# Revit family: Dryer_Weight-Rated_Milnor_M115-Gas
name_source: partatom
category: Mechanical Equipment
units: mm (PartAtom-declared; Revit-internal decimal feet)

## family parameters
Always vertical = No
Classification Number = 23.45.70.11.14.17
Cut with Voids When Loaded = No
Maintain Annotation Orientation = No
Part Type = Normal
Room Calculation Point = No
Round Connector Dimension = Use Radius
Shared = No
Work Plane-Based = Yes

## types (9) — shared parameters
Assembly Code = E1010610
Capacity = 115 lbs Dry Weight
Cylinder Depth = 3' - 5 1/4"
Cylinder Diameter = 3' - 6"
Cylinder Volume = 33.1 CF
Default Elevation = 0' - 0"
Description = Milnor Commercial Laundry Dryer - Gas Model M115 as Specified
Door Base from FF = 2' - 3 1/2"
Door Opening = 2' - 7 3/8"
Door Opening Depth = 3' - 1 7/8"
Door Thickness = 0' - 2"
Electrical CL from CL = 0' - 2"
Electrical CL from FF = 6' - 0 1/2"
Electrical CL from Side = 1' - 1 3/4"
Exhaust CL from FF = 1' - 2 9/16"
Exhaust CL from Side = 0' - 8 1/4"
Exhaust Diameter = 1' - 2"
FSS Water Connection CL from FF = 5' - 7 3/8"
FSS Water Connection Diameter = 0' - 0 3/4"
FSS Water Connection from Side = 0' - 2 3/4"
Gas Connection CL from FF = 6' - 0 1/4"
Gas Connection Diameter = 0' - 1"
Gas Connection from Side = 2' - 9 1/4"
Heat Input = 343000.0 Btu/h
Keynote = 11110
Manufacturer = Pellerin Milnor Corp
Manufacturer Fax = 504-468-3094
Manufacturer Website = http://www.milnor.com
Model = M115
Number of Poles = 1
Phase = 3
Product Data = http://www.arcat.com
Reversing = Yes
Revision = R1_04-2011
Sales Information = http://www.milnor.com
Send Message = http://www.arcat.com
URL = http://www.milnor.com
Unit Depth = 5' - 1 9/16"
Unit Height = 7' - 0"
Unit Weight = 1260
Unit Width = 3' - 10 1/8"
exhaustrad = 0' - 7"
fsswaterrad = 0' - 0 3/8"
gasrad = 0' - 0 1/2"
zero-valued in all types: Expected Lifespan (Years), Maintenance Schedule (Months), Warranty Duration (Years)

## per-type parameters (varying)
| type | Air Flow | Circuit Breaker Size | Frequency | MEP Amperage | Number of Wires | Voltage_MEP |
| 416-50-3ph 15A CB | 1750 CFM | 15 A | 50 Hz | 7 A | 4 | 416 V |
| 400-50-3ph 15A CB | 1750 CFM | 15 A | 50 Hz | 9 A | 4 | 400 V |
| 380-50-3ph 25A CB | 1750 CFM | 25 A | 50 Hz | 9 A | 4 | 380 V |
| 230-50-3ph 15A CB | 1750 CFM | 15 A | 50 Hz | 27 A | 3 | 230 V |
| 575-60-3ph 15A CB | 2100 CFM | 15 A | 60 Hz | 10 A | 3 | 575 V |
| 480-60-3ph 15A CB | 2100 CFM | 15 A | 60 Hz | 8 A | 3 | 480 V |
| 460-60-3ph 15A CB | 2100 CFM | 15 A | 60 Hz | 8 A | 3 | 460 V |
| 240-60-3ph 20A CB | 2100 CFM | 20 A | 60 Hz | 15 A | 3 | 240 V |
| 208-60-3ph 20A CB | 2100 CFM | 20 A | 60 Hz | 15 A | 3 | 208 V |

## geometry (parser evidence)
native form markers: Sweep x1
no freeform markers — native parametric forms only
